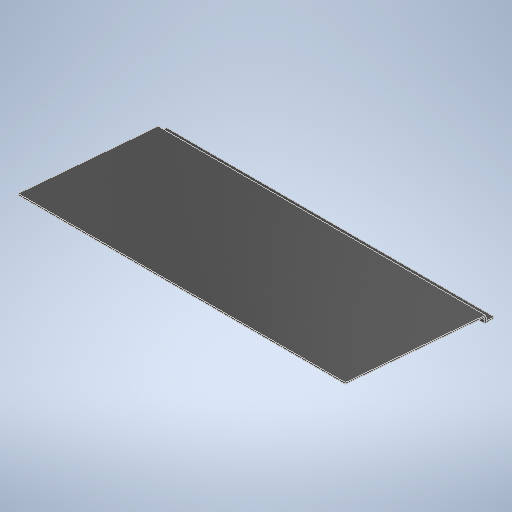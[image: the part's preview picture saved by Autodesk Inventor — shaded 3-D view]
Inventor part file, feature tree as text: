
AUTODESK INVENTOR PART (.ipt)
format: ipt  version: 2025.1 (Build 291241020, 241B)  size: 258,048 bytes
history: native  units: in
note: dims shown in document units (in); Inventor stores cm internally (conversion verified against a paired STEP export)
features: extrude x1, sketch x1
ambient origin geometry x8: Origin, YZ Plane, XZ Plane, XY Plane, X Axis, Y Axis, Z Axis, Center Point
bodies: Body1 (feature_tree)
feature tree (2):
  extrude  "Extrusion2"  Depth=0.125in
  sketch  "Sketch1"  dims[d0=23.408in d1=0.125in d2=0.265in d7=0.125in d8=0.237in d9=1.1431in d10=0.125in d11=0.7449in d12=0.125in d13=12.09in d16=0.125in d18=0.125in d20=12.0907in d21=0.3425in d22=0.125in d23=0.125in d24=0.1549in d25=0.661in d26=28.375in d27=0.0in]
